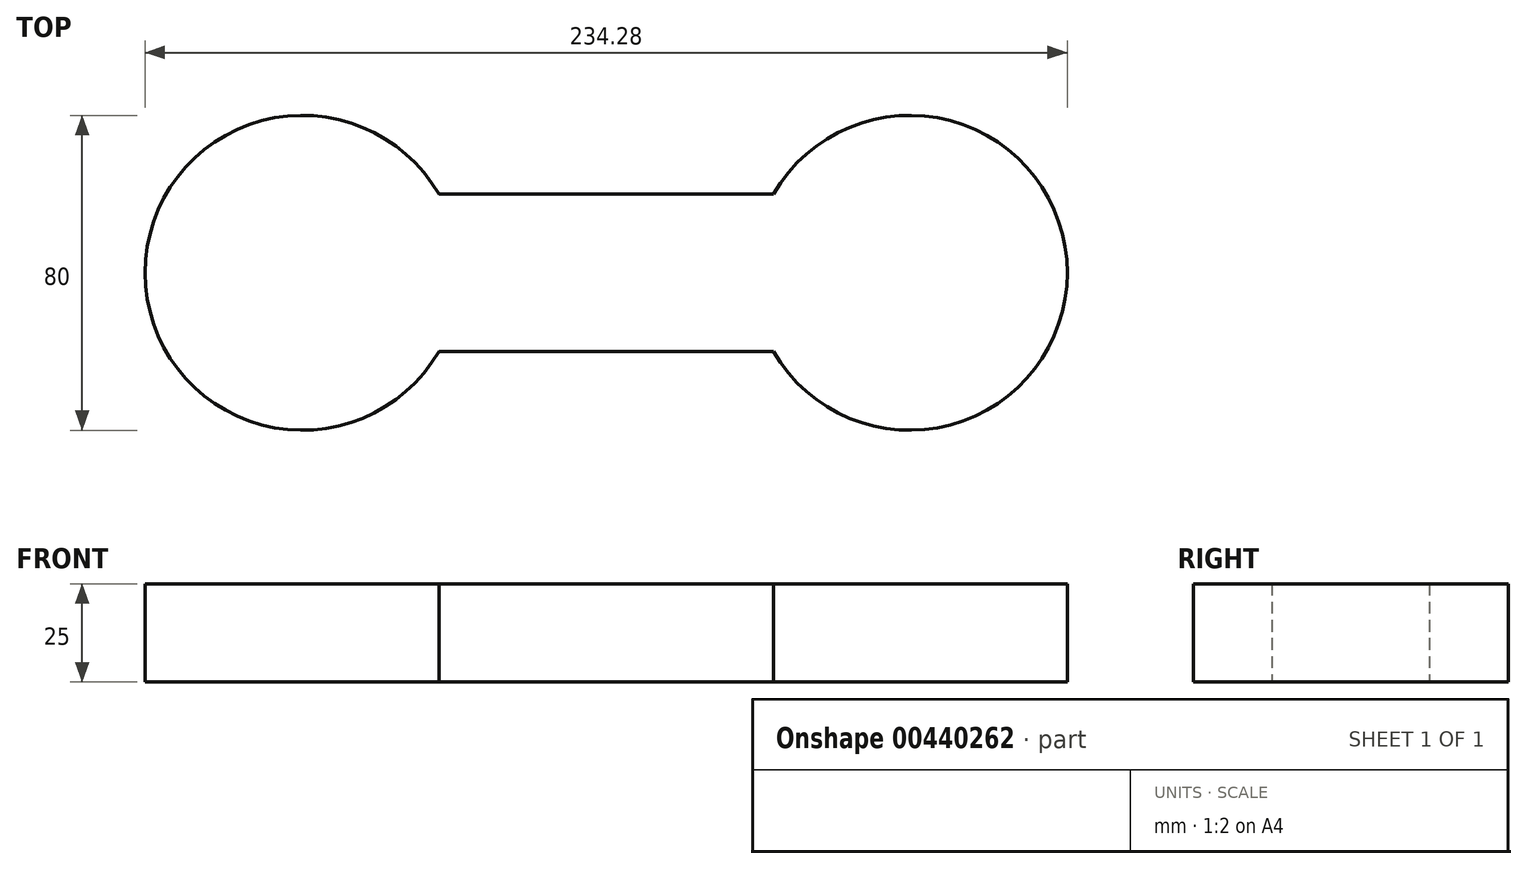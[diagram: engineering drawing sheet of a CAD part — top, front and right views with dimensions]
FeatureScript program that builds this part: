
annotation { "Feature Type Name" : "Feature", "Feature Type Description" : "" }
export const myFeature = defineFeature(function(context is Context, id is Id, definition is map)
    precondition{}
    {
        {
            var Q0;
            Q0=qCreatedBy(makeId("Top.planeOp"),FACE);
            var sketch = newSketch(context, id + "F0", { "sketchPlane" : qUnion([Q0])});
            skLineSegment(sketch, "E0.bottom", {"start": v(-40.52, 22.43) * mm, "end": v(44.48, 22.43) * mm});
            skLineSegment(sketch, "E0.top", {"start": v(-40.52, -17.57) * mm, "end": v(44.48, -17.57) * mm});
            skLineSegment(sketch, "E0.left", {"start": v(-40.52, 22.43) * mm, "end": v(-40.52, -17.57) * mm});
            skLineSegment(sketch, "E0.right", {"start": v(44.48, 22.43) * mm, "end": v(44.48, -17.57) * mm});
            skArc(sketch, "E1", {"start": v(-40.52, 22.43) * mm, "mid": v(-115.16, 2.43) * mm, "end": v(-40.52, -17.57) * mm});
            skArc(sketch, "E2", {"start": v(44.48, -17.57) * mm, "mid": v(119.12, 2.43) * mm, "end": v(44.48, 22.43) * mm});
            skSolve(sketch);
        }
        {
            var Q0;
            Q0=makeQuery(id+"F0.imprint","IMPRINT",FACE,{"disambiguationData":[TD([[makeQuery(id+"F0.imprint","IMPRINT",EDGE,{"derivedFrom":sQuery(id+"F0.wireOp",EDGE,"E0.left")}),-1.0]])]});
            var Q1;
            Q1=makeQuery(id+"F0.imprint","IMPRINT",FACE,{"disambiguationData":[TD([[makeQuery(id+"F0.imprint","IMPRINT",EDGE,{"derivedFrom":sQuery(id+"F0.wireOp",EDGE,"E0.right")}),1.0]])]});
            var Q2;
            Q2=makeQuery(id+"F0.imprint","IMPRINT",FACE,{"disambiguationData":[TD([[makeQuery(id+"F0.imprint","IMPRINT",EDGE,{"derivedFrom":sQuery(id+"F0.wireOp",EDGE,"E0.bottom")}),-1.0]])]});
            extrude(context, id + "F1", {"entities" : qUnion([Q0, Q1, Q2]), "depth" : 25 * mm});
        }
    });
